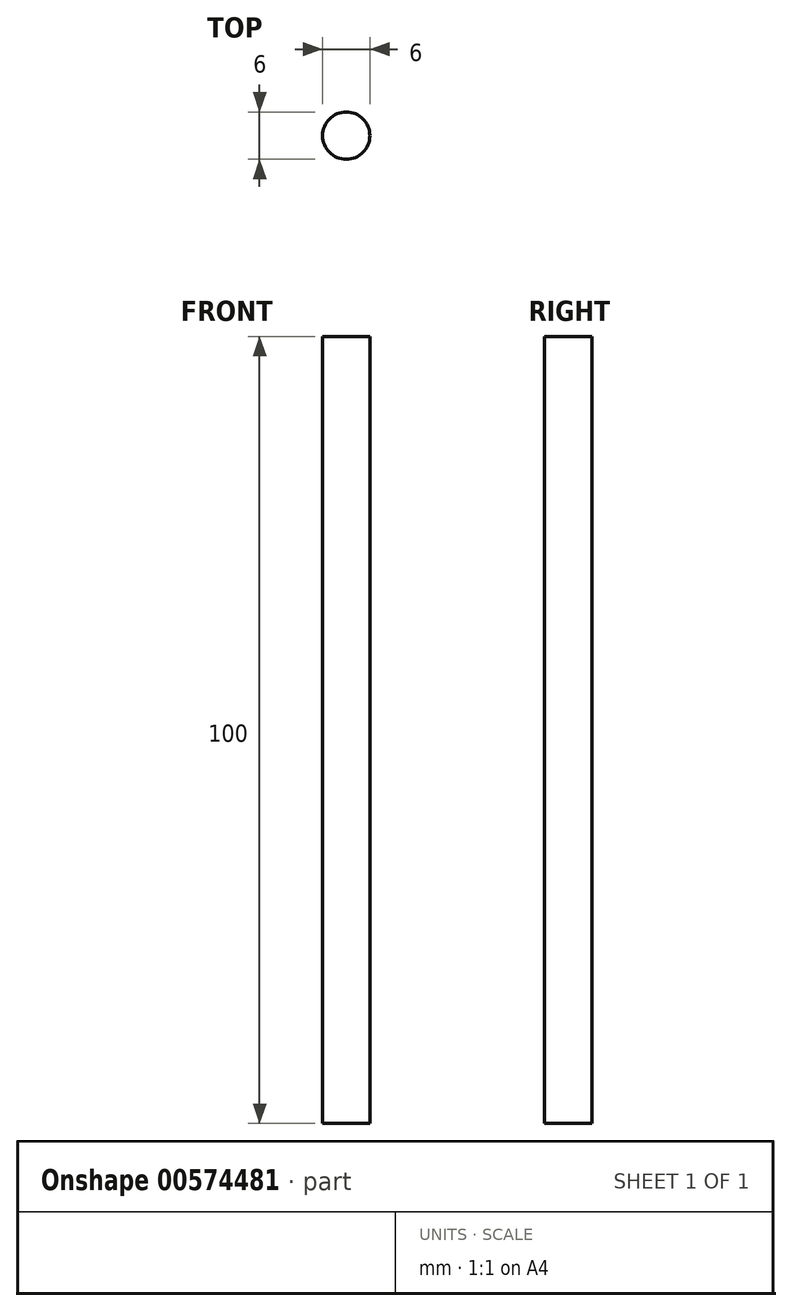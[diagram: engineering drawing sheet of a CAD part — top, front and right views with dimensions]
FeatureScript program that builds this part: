
annotation { "Feature Type Name" : "Feature", "Feature Type Description" : "" }
export const myFeature = defineFeature(function(context is Context, id is Id, definition is map)
    precondition{}
    {
        {
            var Q0;
            Q0=qCreatedBy(makeId("Top.planeOp"),FACE);
            var sketch = newSketch(context, id + "F0", { "sketchPlane" : qUnion([Q0])});
            skCircle(sketch, "E0", {"center": v(0, 0) * mm, "radius": 3 * mm});
            skSolve(sketch);
        }
        {
            var Q0;
            Q0=makeQuery(id+"F0.imprint","IMPRINT",FACE,{"disambiguationData":[TD([[makeQuery(id+"F0.imprint","IMPRINT",EDGE,{"derivedFrom":sQuery(id+"F0.wireOp",EDGE,"E0")}),1.0]])]});
            extrude(context, id + "F1", {"entities" : qUnion([Q0]), "depth" : 100 * mm, "offsetDistance" : 25 * mm});
        }
    });
